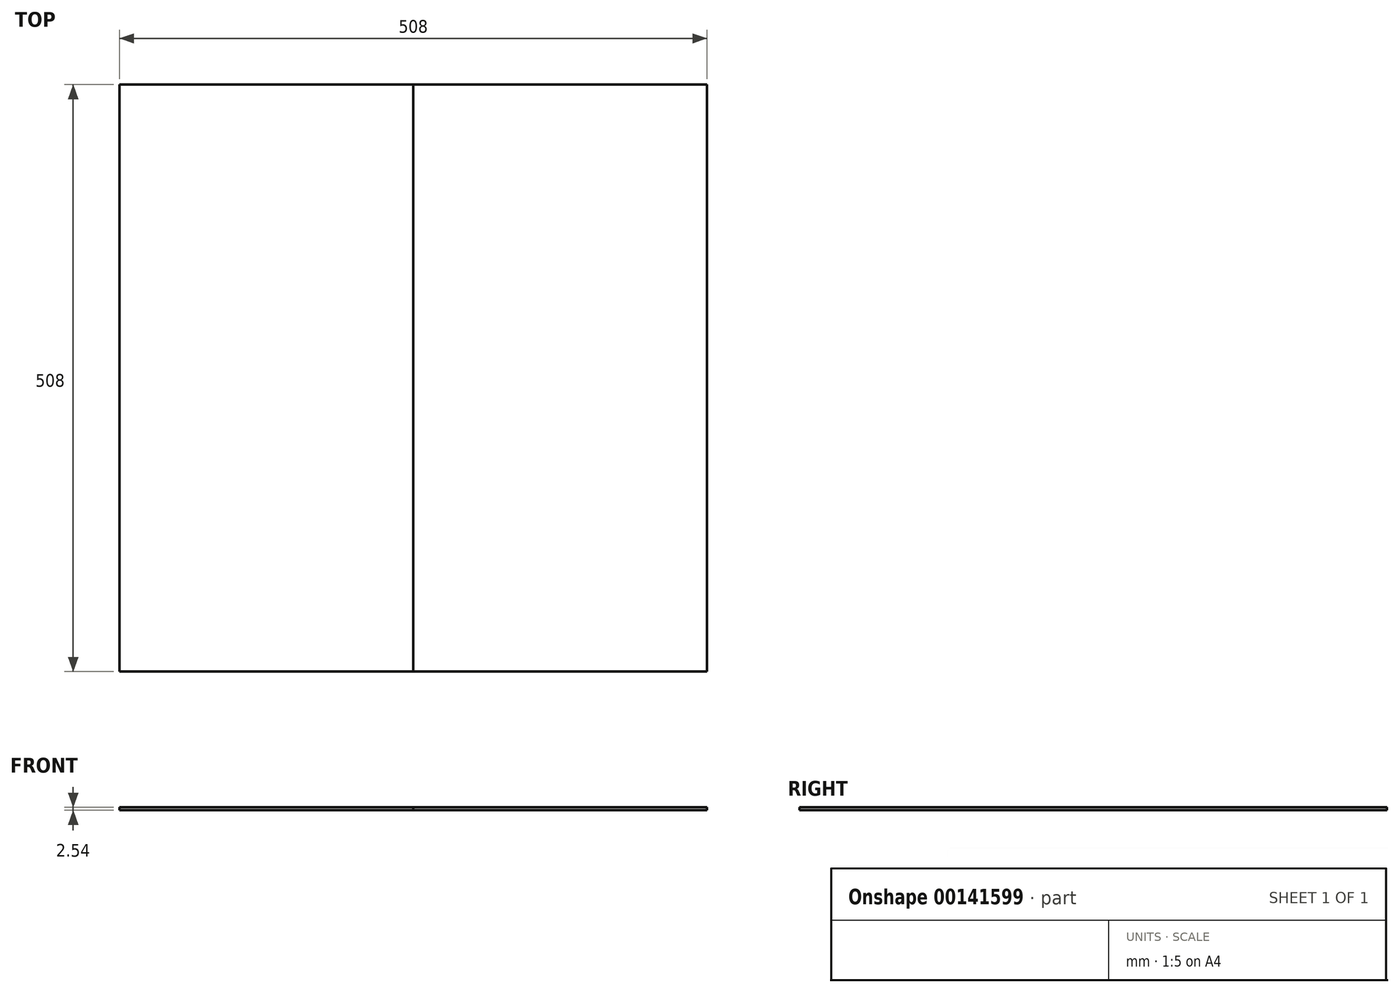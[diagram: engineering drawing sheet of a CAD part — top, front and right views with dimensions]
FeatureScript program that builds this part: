
annotation { "Feature Type Name" : "Feature", "Feature Type Description" : "" }
export const myFeature = defineFeature(function(context is Context, id is Id, definition is map)
    precondition{}
    {
        {
            var Q0;
            Q0=qCreatedBy(makeId("Top.planeOp"),FACE);
            var sketch = newSketch(context, id + "F0", { "sketchPlane" : qUnion([Q0])});
            skLineSegment(sketch, "E0.top", {"start": v(0, 254) * mm, "end": v(-254, 254) * mm});
            skLineSegment(sketch, "E0.right", {"start": v(-254, 0) * mm, "end": v(-254, 254) * mm});
            skLineSegment(sketch, "E1.MirrorCS", {"start": v(0, 254) * mm, "end": v(254, 254) * mm});
            skLineSegment(sketch, "E2.MirrorCS", {"start": v(254, 0) * mm, "end": v(254, 254) * mm});
            skLineSegment(sketch, "E3.MirrorCS", {"start": v(0, -254) * mm, "end": v(-254, -254) * mm});
            skLineSegment(sketch, "E4.MirrorCS", {"start": v(0, -254) * mm, "end": v(254, -254) * mm});
            skLineSegment(sketch, "E5.MirrorCS", {"start": v(254, 0) * mm, "end": v(254, -254) * mm});
            skLineSegment(sketch, "E6.MirrorCS", {"start": v(-254, 0) * mm, "end": v(-254, -254) * mm});
            skLineSegment(sketch, "E7", {"start": v(0, 254) * mm, "end": v(0, -254) * mm});
            skSolve(sketch);
        }
        {
            var Q0;
            Q0=makeQuery(id+"F0.imprint","IMPRINT",FACE,{"disambiguationData":[TD([[makeQuery(id+"F0.imprint","IMPRINT",EDGE,{"derivedFrom":sQuery(id+"F0.wireOp",EDGE,"E0.top")}),1.0]])]});
            extrude(context, id + "F1", {"entities" : qUnion([Q0]), "depth" : 2.54 * mm});
        }
        {
            var Q0;
            Q0=makeQuery(id+"F0.imprint","IMPRINT",FACE,{"disambiguationData":[TD([[makeQuery(id+"F0.imprint","IMPRINT",EDGE,{"derivedFrom":sQuery(id+"F0.wireOp",EDGE,"E1.MirrorCS")}),-1.0]])]});
            extrude(context, id + "F2", {"entities" : qUnion([Q0]), "depth" : 2.54 * mm});
        }
    });
